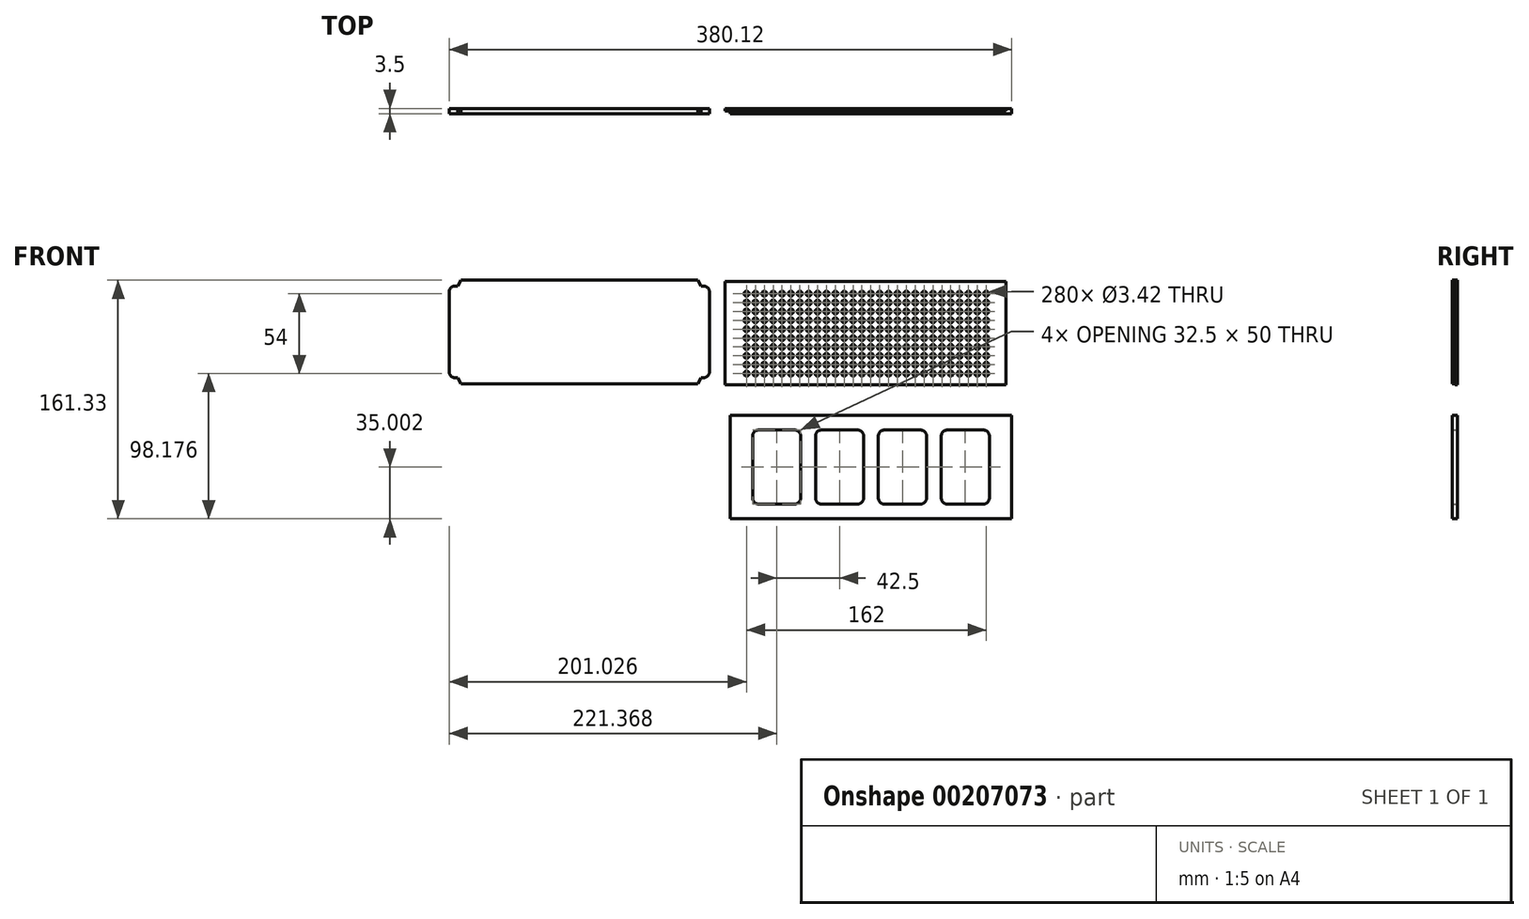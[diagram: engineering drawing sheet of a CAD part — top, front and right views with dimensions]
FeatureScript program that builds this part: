
annotation { "Feature Type Name" : "Feature", "Feature Type Description" : "" }
export const myFeature = defineFeature(function(context is Context, id is Id, definition is map)
    precondition{}
    {
        {
            var Q0;
            Q0=qCreatedBy(makeId("Front.planeOp"),FACE);
            var sketch = newSketch(context, id + "F0", { "sketchPlane" : qUnion([Q0])});
            skLineSegment(sketch, "E0", {"start": v(-6.1, -37) * mm, "end": v(73.9, -37) * mm});
            skLineSegment(sketch, "E1", {"start": v(73.9, -37) * mm, "end": v(76.2, -33) * mm});
            skLineSegment(sketch, "E2", {"start": v(76.2, -33) * mm, "end": v(77.9, -33) * mm});
            skLineSegment(sketch, "E3", {"start": v(77.9, -33) * mm, "end": v(77.9, -33) * mm});
            skLineSegment(sketch, "E4", {"start": v(81.9, -29) * mm, "end": v(81.9, -29) * mm});
            skLineSegment(sketch, "E5", {"start": v(81.9, -29) * mm, "end": v(81.9, 25) * mm});
            skLineSegment(sketch, "E6", {"start": v(77.9, 29) * mm, "end": v(77.9, 29) * mm});
            skLineSegment(sketch, "E7", {"start": v(77.9, 29) * mm, "end": v(76.2, 29) * mm});
            skLineSegment(sketch, "E8", {"start": v(76.2, 29) * mm, "end": v(73.9, 33) * mm});
            skLineSegment(sketch, "E9", {"start": v(73.9, 33) * mm, "end": v(-6.1, 33) * mm});
            skLineSegment(sketch, "E10", {"start": v(-6.1, 33) * mm, "end": v(-6.1, -37) * mm});
            skPoint(sketch, "E11.visualSharp", {"position": v(81.9, -33) * mm});
            skArc(sketch, "E11.filletArc", {"start": v(77.9, -33) * mm, "mid": v(80.72, -31.83) * mm, "end": v(81.9, -29) * mm});
            skArc(sketch, "E12.filletArc", {"start": v(81.9, 25) * mm, "mid": v(80.72, 27.83) * mm, "end": v(77.9, 29) * mm});
            skSolve(sketch);
        }
        {
            var Q0;
            Q0=makeQuery(id+"F0.imprint","IMPRINT",FACE,{"disambiguationData":[TD([[makeQuery(id+"F0.imprint","IMPRINT",EDGE,{"derivedFrom":sQuery(id+"F0.wireOp",EDGE,"E0")}),1.0]])]});
            extrude(context, id + "F1", {"entities" : qUnion([Q0]), "depth" : 3.5 * mm});
        }
        {
            var Q0;
            Q0=makeQuery(id+"F1.opExtrude","SWEPT_BODY",BODY,{"disambiguationData":[OSD([sQuery(id+"F0.wireOp",EDGE,"E0"),sQuery(id+"F0.wireOp",EDGE,"E1"),sQuery(id+"F0.wireOp",EDGE,"E2"),sQuery(id+"F0.wireOp",EDGE,"E5"),sQuery(id+"F0.wireOp",EDGE,"E7"),sQuery(id+"F0.wireOp",EDGE,"E8"),sQuery(id+"F0.wireOp",EDGE,"E9"),sQuery(id+"F0.wireOp",EDGE,"E10"),sQuery(id+"F0.wireOp",EDGE,"E11.filletArc"),sQuery(id+"F0.wireOp",EDGE,"E12.filletArc")])]});
            var Q1;
            Q1=makeQuery(id+"F1.opExtrude","SWEPT_FACE",FACE,{"disambiguationData":[OSD([sQuery(id+"F0.wireOp",EDGE,"E10")])]});
            mirror(context, id + "F2", {"operationType" : NewBodyOperationType.ADD, "entities" : qUnion([Q0]), "mirrorPlane" : qUnion([Q1])});
        }
        {
            var Q0;
            Q0=qCreatedBy(makeId("Front.planeOp"),FACE);
            var sketch = newSketch(context, id + "F3", { "sketchPlane" : qUnion([Q0])});
            skLineSegment(sketch, "E13.bottom", {"start": v(92.39, 32.26) * mm, "end": v(282.39, 32.26) * mm});
            skLineSegment(sketch, "E13.top", {"start": v(92.39, -37.74) * mm, "end": v(282.39, -37.74) * mm});
            skLineSegment(sketch, "E13.left", {"start": v(92.39, 32.26) * mm, "end": v(92.39, -37.74) * mm});
            skLineSegment(sketch, "E13.right", {"start": v(282.39, 32.26) * mm, "end": v(282.39, -37.74) * mm});
            skSolve(sketch);
        }
        {
            var Q0;
            Q0=makeQuery(id+"F3.imprint","IMPRINT",FACE,{"disambiguationData":[TD([[makeQuery(id+"F3.imprint","IMPRINT",EDGE,{"derivedFrom":sQuery(id+"F3.wireOp",EDGE,"E13.bottom")}),-1.0]])]});
            extrude(context, id + "F4", {"entities" : qUnion([Q0]), "depth" : 1.5 * mm});
        }
        {
            var Q0;
            Q0=makeQuery(id+"F4.opExtrude","CAP_FACE",FACE,{"disambiguationData":[OSD([sQuery(id+"F3.wireOp",EDGE,"E13.bottom"),sQuery(id+"F3.wireOp",EDGE,"E13.top"),sQuery(id+"F3.wireOp",EDGE,"E13.left"),sQuery(id+"F3.wireOp",EDGE,"E13.right")])],"isStart":false});
            var sketch = newSketch(context, id + "F5", { "sketchPlane" : qUnion([Q0])});
            skCircle(sketch, "E14", {"center": v(106.92, 23.85) * mm, "radius": 1.7 * mm});
            skCircle(sketch, "E15.0.1.0", {"center": v(106.92, 17.85) * mm, "radius": 1.7 * mm});
            skCircle(sketch, "E15.0.2.0", {"center": v(106.92, 11.85) * mm, "radius": 1.7 * mm});
            skCircle(sketch, "E15.0.3.0", {"center": v(106.92, 5.85) * mm, "radius": 1.7 * mm});
            skCircle(sketch, "E15.0.4.0", {"center": v(106.92, -0.15) * mm, "radius": 1.7 * mm});
            skCircle(sketch, "E15.0.5.0", {"center": v(106.92, -6.15) * mm, "radius": 1.7 * mm});
            skCircle(sketch, "E15.0.6.0", {"center": v(106.92, -12.15) * mm, "radius": 1.7 * mm});
            skCircle(sketch, "E15.0.7.0", {"center": v(106.92, -18.15) * mm, "radius": 1.7 * mm});
            skCircle(sketch, "E15.0.8.0", {"center": v(106.92, -24.15) * mm, "radius": 1.7 * mm});
            skCircle(sketch, "E15.0.9.0", {"center": v(106.92, -30.15) * mm, "radius": 1.7 * mm});
            skCircle(sketch, "E15.1.0.0", {"center": v(112.92, 23.85) * mm, "radius": 1.7 * mm});
            skCircle(sketch, "E15.1.1.0", {"center": v(112.92, 17.85) * mm, "radius": 1.7 * mm});
            skCircle(sketch, "E15.1.2.0", {"center": v(112.92, 11.85) * mm, "radius": 1.7 * mm});
            skCircle(sketch, "E15.1.3.0", {"center": v(112.92, 5.85) * mm, "radius": 1.7 * mm});
            skCircle(sketch, "E15.1.4.0", {"center": v(112.92, -0.15) * mm, "radius": 1.7 * mm});
            skCircle(sketch, "E15.1.5.0", {"center": v(112.92, -6.15) * mm, "radius": 1.7 * mm});
            skCircle(sketch, "E15.1.6.0", {"center": v(112.92, -12.15) * mm, "radius": 1.7 * mm});
            skCircle(sketch, "E15.1.7.0", {"center": v(112.92, -18.15) * mm, "radius": 1.7 * mm});
            skCircle(sketch, "E15.1.8.0", {"center": v(112.92, -24.15) * mm, "radius": 1.7 * mm});
            skCircle(sketch, "E15.1.9.0", {"center": v(112.92, -30.15) * mm, "radius": 1.7 * mm});
            skCircle(sketch, "E15.2.0.0", {"center": v(118.92, 23.85) * mm, "radius": 1.7 * mm});
            skCircle(sketch, "E15.2.1.0", {"center": v(118.92, 17.85) * mm, "radius": 1.7 * mm});
            skCircle(sketch, "E15.2.2.0", {"center": v(118.92, 11.85) * mm, "radius": 1.7 * mm});
            skCircle(sketch, "E15.2.3.0", {"center": v(118.92, 5.85) * mm, "radius": 1.7 * mm});
            skCircle(sketch, "E15.2.4.0", {"center": v(118.92, -0.15) * mm, "radius": 1.7 * mm});
            skCircle(sketch, "E15.2.5.0", {"center": v(118.92, -6.15) * mm, "radius": 1.7 * mm});
            skCircle(sketch, "E15.2.6.0", {"center": v(118.92, -12.15) * mm, "radius": 1.7 * mm});
            skCircle(sketch, "E15.2.7.0", {"center": v(118.92, -18.15) * mm, "radius": 1.7 * mm});
            skCircle(sketch, "E15.2.8.0", {"center": v(118.92, -24.15) * mm, "radius": 1.7 * mm});
            skCircle(sketch, "E15.2.9.0", {"center": v(118.92, -30.15) * mm, "radius": 1.7 * mm});
            skCircle(sketch, "E15.3.0.0", {"center": v(124.92, 23.85) * mm, "radius": 1.7 * mm});
            skCircle(sketch, "E15.3.1.0", {"center": v(124.92, 17.85) * mm, "radius": 1.7 * mm});
            skCircle(sketch, "E15.3.2.0", {"center": v(124.92, 11.85) * mm, "radius": 1.7 * mm});
            skCircle(sketch, "E15.3.3.0", {"center": v(124.92, 5.85) * mm, "radius": 1.7 * mm});
            skCircle(sketch, "E15.3.4.0", {"center": v(124.92, -0.15) * mm, "radius": 1.7 * mm});
            skCircle(sketch, "E15.3.5.0", {"center": v(124.92, -6.15) * mm, "radius": 1.7 * mm});
            skCircle(sketch, "E15.3.6.0", {"center": v(124.92, -12.15) * mm, "radius": 1.7 * mm});
            skCircle(sketch, "E15.3.7.0", {"center": v(124.92, -18.15) * mm, "radius": 1.7 * mm});
            skCircle(sketch, "E15.3.8.0", {"center": v(124.92, -24.15) * mm, "radius": 1.7 * mm});
            skCircle(sketch, "E15.3.9.0", {"center": v(124.92, -30.15) * mm, "radius": 1.7 * mm});
            skCircle(sketch, "E15.4.0.0", {"center": v(130.92, 23.85) * mm, "radius": 1.7 * mm});
            skCircle(sketch, "E15.4.1.0", {"center": v(130.92, 17.85) * mm, "radius": 1.7 * mm});
            skCircle(sketch, "E15.4.2.0", {"center": v(130.92, 11.85) * mm, "radius": 1.7 * mm});
            skCircle(sketch, "E15.4.3.0", {"center": v(130.92, 5.85) * mm, "radius": 1.7 * mm});
            skCircle(sketch, "E15.4.4.0", {"center": v(130.92, -0.15) * mm, "radius": 1.7 * mm});
            skCircle(sketch, "E15.4.5.0", {"center": v(130.92, -6.15) * mm, "radius": 1.7 * mm});
            skCircle(sketch, "E15.4.6.0", {"center": v(130.92, -12.15) * mm, "radius": 1.7 * mm});
            skCircle(sketch, "E15.4.7.0", {"center": v(130.92, -18.15) * mm, "radius": 1.7 * mm});
            skCircle(sketch, "E15.4.8.0", {"center": v(130.92, -24.15) * mm, "radius": 1.7 * mm});
            skCircle(sketch, "E15.4.9.0", {"center": v(130.92, -30.15) * mm, "radius": 1.7 * mm});
            skCircle(sketch, "E15.5.0.0", {"center": v(136.92, 23.85) * mm, "radius": 1.7 * mm});
            skCircle(sketch, "E15.5.1.0", {"center": v(136.92, 17.85) * mm, "radius": 1.7 * mm});
            skCircle(sketch, "E15.5.2.0", {"center": v(136.92, 11.85) * mm, "radius": 1.7 * mm});
            skCircle(sketch, "E15.5.3.0", {"center": v(136.92, 5.85) * mm, "radius": 1.7 * mm});
            skCircle(sketch, "E15.5.4.0", {"center": v(136.92, -0.15) * mm, "radius": 1.7 * mm});
            skCircle(sketch, "E15.5.5.0", {"center": v(136.92, -6.15) * mm, "radius": 1.7 * mm});
            skCircle(sketch, "E15.5.6.0", {"center": v(136.92, -12.15) * mm, "radius": 1.7 * mm});
            skCircle(sketch, "E15.5.7.0", {"center": v(136.92, -18.15) * mm, "radius": 1.7 * mm});
            skCircle(sketch, "E15.5.8.0", {"center": v(136.92, -24.15) * mm, "radius": 1.7 * mm});
            skCircle(sketch, "E15.5.9.0", {"center": v(136.92, -30.15) * mm, "radius": 1.7 * mm});
            skCircle(sketch, "E15.6.0.0", {"center": v(142.92, 23.85) * mm, "radius": 1.7 * mm});
            skCircle(sketch, "E15.6.1.0", {"center": v(142.92, 17.85) * mm, "radius": 1.7 * mm});
            skCircle(sketch, "E15.6.2.0", {"center": v(142.92, 11.85) * mm, "radius": 1.7 * mm});
            skCircle(sketch, "E15.6.3.0", {"center": v(142.92, 5.85) * mm, "radius": 1.7 * mm});
            skCircle(sketch, "E15.6.4.0", {"center": v(142.92, -0.15) * mm, "radius": 1.7 * mm});
            skCircle(sketch, "E15.6.5.0", {"center": v(142.92, -6.15) * mm, "radius": 1.7 * mm});
            skCircle(sketch, "E15.6.6.0", {"center": v(142.92, -12.15) * mm, "radius": 1.7 * mm});
            skCircle(sketch, "E15.6.7.0", {"center": v(142.92, -18.15) * mm, "radius": 1.7 * mm});
            skCircle(sketch, "E15.6.8.0", {"center": v(142.92, -24.15) * mm, "radius": 1.7 * mm});
            skCircle(sketch, "E15.6.9.0", {"center": v(142.92, -30.15) * mm, "radius": 1.7 * mm});
            skCircle(sketch, "E15.7.0.0", {"center": v(148.92, 23.85) * mm, "radius": 1.7 * mm});
            skCircle(sketch, "E15.7.1.0", {"center": v(148.92, 17.85) * mm, "radius": 1.7 * mm});
            skCircle(sketch, "E15.7.2.0", {"center": v(148.92, 11.85) * mm, "radius": 1.7 * mm});
            skCircle(sketch, "E15.7.3.0", {"center": v(148.92, 5.85) * mm, "radius": 1.7 * mm});
            skCircle(sketch, "E15.7.4.0", {"center": v(148.92, -0.15) * mm, "radius": 1.7 * mm});
            skCircle(sketch, "E15.7.5.0", {"center": v(148.92, -6.15) * mm, "radius": 1.7 * mm});
            skCircle(sketch, "E15.7.6.0", {"center": v(148.92, -12.15) * mm, "radius": 1.7 * mm});
            skCircle(sketch, "E15.7.7.0", {"center": v(148.92, -18.15) * mm, "radius": 1.7 * mm});
            skCircle(sketch, "E15.7.8.0", {"center": v(148.92, -24.15) * mm, "radius": 1.7 * mm});
            skCircle(sketch, "E15.7.9.0", {"center": v(148.92, -30.15) * mm, "radius": 1.7 * mm});
            skCircle(sketch, "E15.8.0.0", {"center": v(154.92, 23.85) * mm, "radius": 1.7 * mm});
            skCircle(sketch, "E15.8.1.0", {"center": v(154.92, 17.85) * mm, "radius": 1.7 * mm});
            skCircle(sketch, "E15.8.2.0", {"center": v(154.92, 11.85) * mm, "radius": 1.7 * mm});
            skCircle(sketch, "E15.8.3.0", {"center": v(154.92, 5.85) * mm, "radius": 1.7 * mm});
            skCircle(sketch, "E15.8.4.0", {"center": v(154.92, -0.15) * mm, "radius": 1.7 * mm});
            skCircle(sketch, "E15.8.5.0", {"center": v(154.92, -6.15) * mm, "radius": 1.7 * mm});
            skCircle(sketch, "E15.8.6.0", {"center": v(154.92, -12.15) * mm, "radius": 1.7 * mm});
            skCircle(sketch, "E15.8.7.0", {"center": v(154.92, -18.15) * mm, "radius": 1.7 * mm});
            skCircle(sketch, "E15.8.8.0", {"center": v(154.92, -24.15) * mm, "radius": 1.7 * mm});
            skCircle(sketch, "E15.8.9.0", {"center": v(154.92, -30.15) * mm, "radius": 1.7 * mm});
            skCircle(sketch, "E15.9.0.0", {"center": v(160.92, 23.85) * mm, "radius": 1.7 * mm});
            skCircle(sketch, "E15.9.1.0", {"center": v(160.92, 17.85) * mm, "radius": 1.7 * mm});
            skCircle(sketch, "E15.9.2.0", {"center": v(160.92, 11.85) * mm, "radius": 1.7 * mm});
            skCircle(sketch, "E15.9.3.0", {"center": v(160.92, 5.85) * mm, "radius": 1.7 * mm});
            skCircle(sketch, "E15.9.4.0", {"center": v(160.92, -0.15) * mm, "radius": 1.7 * mm});
            skCircle(sketch, "E15.9.5.0", {"center": v(160.92, -6.15) * mm, "radius": 1.7 * mm});
            skCircle(sketch, "E15.9.6.0", {"center": v(160.92, -12.15) * mm, "radius": 1.7 * mm});
            skCircle(sketch, "E15.9.7.0", {"center": v(160.92, -18.15) * mm, "radius": 1.7 * mm});
            skCircle(sketch, "E15.9.8.0", {"center": v(160.92, -24.15) * mm, "radius": 1.7 * mm});
            skCircle(sketch, "E15.9.9.0", {"center": v(160.92, -30.15) * mm, "radius": 1.7 * mm});
            skCircle(sketch, "E15.10.0.0", {"center": v(166.92, 23.85) * mm, "radius": 1.7 * mm});
            skCircle(sketch, "E15.10.1.0", {"center": v(166.92, 17.85) * mm, "radius": 1.7 * mm});
            skCircle(sketch, "E15.10.2.0", {"center": v(166.92, 11.85) * mm, "radius": 1.7 * mm});
            skCircle(sketch, "E15.10.3.0", {"center": v(166.92, 5.85) * mm, "radius": 1.7 * mm});
            skCircle(sketch, "E15.10.4.0", {"center": v(166.92, -0.15) * mm, "radius": 1.7 * mm});
            skCircle(sketch, "E15.10.5.0", {"center": v(166.92, -6.15) * mm, "radius": 1.7 * mm});
            skCircle(sketch, "E15.10.6.0", {"center": v(166.92, -12.15) * mm, "radius": 1.7 * mm});
            skCircle(sketch, "E15.10.7.0", {"center": v(166.92, -18.15) * mm, "radius": 1.7 * mm});
            skCircle(sketch, "E15.10.8.0", {"center": v(166.92, -24.15) * mm, "radius": 1.7 * mm});
            skCircle(sketch, "E15.10.9.0", {"center": v(166.92, -30.15) * mm, "radius": 1.7 * mm});
            skCircle(sketch, "E15.11.0.0", {"center": v(172.92, 23.85) * mm, "radius": 1.7 * mm});
            skCircle(sketch, "E15.11.1.0", {"center": v(172.92, 17.85) * mm, "radius": 1.7 * mm});
            skCircle(sketch, "E15.11.2.0", {"center": v(172.92, 11.85) * mm, "radius": 1.7 * mm});
            skCircle(sketch, "E15.11.3.0", {"center": v(172.92, 5.85) * mm, "radius": 1.7 * mm});
            skCircle(sketch, "E15.11.4.0", {"center": v(172.92, -0.15) * mm, "radius": 1.7 * mm});
            skCircle(sketch, "E15.11.5.0", {"center": v(172.92, -6.15) * mm, "radius": 1.7 * mm});
            skCircle(sketch, "E15.11.6.0", {"center": v(172.92, -12.15) * mm, "radius": 1.7 * mm});
            skCircle(sketch, "E15.11.7.0", {"center": v(172.92, -18.15) * mm, "radius": 1.7 * mm});
            skCircle(sketch, "E15.11.8.0", {"center": v(172.92, -24.15) * mm, "radius": 1.7 * mm});
            skCircle(sketch, "E15.11.9.0", {"center": v(172.92, -30.15) * mm, "radius": 1.7 * mm});
            skCircle(sketch, "E15.12.0.0", {"center": v(178.92, 23.85) * mm, "radius": 1.7 * mm});
            skCircle(sketch, "E15.12.1.0", {"center": v(178.92, 17.85) * mm, "radius": 1.7 * mm});
            skCircle(sketch, "E15.12.2.0", {"center": v(178.92, 11.85) * mm, "radius": 1.7 * mm});
            skCircle(sketch, "E15.12.3.0", {"center": v(178.92, 5.85) * mm, "radius": 1.7 * mm});
            skCircle(sketch, "E15.12.4.0", {"center": v(178.92, -0.15) * mm, "radius": 1.7 * mm});
            skCircle(sketch, "E15.12.5.0", {"center": v(178.92, -6.15) * mm, "radius": 1.7 * mm});
            skCircle(sketch, "E15.12.6.0", {"center": v(178.92, -12.15) * mm, "radius": 1.7 * mm});
            skCircle(sketch, "E15.12.7.0", {"center": v(178.92, -18.15) * mm, "radius": 1.7 * mm});
            skCircle(sketch, "E15.12.8.0", {"center": v(178.92, -24.15) * mm, "radius": 1.7 * mm});
            skCircle(sketch, "E15.12.9.0", {"center": v(178.92, -30.15) * mm, "radius": 1.7 * mm});
            skCircle(sketch, "E15.13.0.0", {"center": v(184.92, 23.85) * mm, "radius": 1.7 * mm});
            skCircle(sketch, "E15.13.1.0", {"center": v(184.92, 17.85) * mm, "radius": 1.7 * mm});
            skCircle(sketch, "E15.13.2.0", {"center": v(184.92, 11.85) * mm, "radius": 1.7 * mm});
            skCircle(sketch, "E15.13.3.0", {"center": v(184.92, 5.85) * mm, "radius": 1.7 * mm});
            skCircle(sketch, "E15.13.4.0", {"center": v(184.92, -0.15) * mm, "radius": 1.7 * mm});
            skCircle(sketch, "E15.13.5.0", {"center": v(184.92, -6.15) * mm, "radius": 1.7 * mm});
            skCircle(sketch, "E15.13.6.0", {"center": v(184.92, -12.15) * mm, "radius": 1.7 * mm});
            skCircle(sketch, "E15.13.7.0", {"center": v(184.92, -18.15) * mm, "radius": 1.7 * mm});
            skCircle(sketch, "E15.13.8.0", {"center": v(184.92, -24.15) * mm, "radius": 1.7 * mm});
            skCircle(sketch, "E15.13.9.0", {"center": v(184.92, -30.15) * mm, "radius": 1.7 * mm});
            skCircle(sketch, "E15.14.0.0", {"center": v(190.92, 23.85) * mm, "radius": 1.7 * mm});
            skCircle(sketch, "E15.14.1.0", {"center": v(190.92, 17.85) * mm, "radius": 1.7 * mm});
            skCircle(sketch, "E15.14.2.0", {"center": v(190.92, 11.85) * mm, "radius": 1.7 * mm});
            skCircle(sketch, "E15.14.3.0", {"center": v(190.92, 5.85) * mm, "radius": 1.7 * mm});
            skCircle(sketch, "E15.14.4.0", {"center": v(190.92, -0.15) * mm, "radius": 1.7 * mm});
            skCircle(sketch, "E15.14.5.0", {"center": v(190.92, -6.15) * mm, "radius": 1.7 * mm});
            skCircle(sketch, "E15.14.6.0", {"center": v(190.92, -12.15) * mm, "radius": 1.7 * mm});
            skCircle(sketch, "E15.14.7.0", {"center": v(190.92, -18.15) * mm, "radius": 1.7 * mm});
            skCircle(sketch, "E15.14.8.0", {"center": v(190.92, -24.15) * mm, "radius": 1.7 * mm});
            skCircle(sketch, "E15.14.9.0", {"center": v(190.92, -30.15) * mm, "radius": 1.7 * mm});
            skCircle(sketch, "E15.15.0.0", {"center": v(196.92, 23.85) * mm, "radius": 1.7 * mm});
            skCircle(sketch, "E15.15.1.0", {"center": v(196.92, 17.85) * mm, "radius": 1.7 * mm});
            skCircle(sketch, "E15.15.2.0", {"center": v(196.92, 11.85) * mm, "radius": 1.7 * mm});
            skCircle(sketch, "E15.15.3.0", {"center": v(196.92, 5.85) * mm, "radius": 1.7 * mm});
            skCircle(sketch, "E15.15.4.0", {"center": v(196.92, -0.15) * mm, "radius": 1.7 * mm});
            skCircle(sketch, "E15.15.5.0", {"center": v(196.92, -6.15) * mm, "radius": 1.7 * mm});
            skCircle(sketch, "E15.15.6.0", {"center": v(196.92, -12.15) * mm, "radius": 1.7 * mm});
            skCircle(sketch, "E15.15.7.0", {"center": v(196.92, -18.15) * mm, "radius": 1.7 * mm});
            skCircle(sketch, "E15.15.8.0", {"center": v(196.92, -24.15) * mm, "radius": 1.7 * mm});
            skCircle(sketch, "E15.15.9.0", {"center": v(196.92, -30.15) * mm, "radius": 1.7 * mm});
            skCircle(sketch, "E15.16.0.0", {"center": v(202.92, 23.85) * mm, "radius": 1.7 * mm});
            skCircle(sketch, "E15.16.1.0", {"center": v(202.92, 17.85) * mm, "radius": 1.7 * mm});
            skCircle(sketch, "E15.16.2.0", {"center": v(202.92, 11.85) * mm, "radius": 1.7 * mm});
            skCircle(sketch, "E15.16.3.0", {"center": v(202.92, 5.85) * mm, "radius": 1.7 * mm});
            skCircle(sketch, "E15.16.4.0", {"center": v(202.92, -0.15) * mm, "radius": 1.7 * mm});
            skCircle(sketch, "E15.16.5.0", {"center": v(202.92, -6.15) * mm, "radius": 1.7 * mm});
            skCircle(sketch, "E15.16.6.0", {"center": v(202.92, -12.15) * mm, "radius": 1.7 * mm});
            skCircle(sketch, "E15.16.7.0", {"center": v(202.92, -18.15) * mm, "radius": 1.7 * mm});
            skCircle(sketch, "E15.16.8.0", {"center": v(202.92, -24.15) * mm, "radius": 1.7 * mm});
            skCircle(sketch, "E15.16.9.0", {"center": v(202.92, -30.15) * mm, "radius": 1.7 * mm});
            skCircle(sketch, "E15.17.0.0", {"center": v(208.92, 23.85) * mm, "radius": 1.7 * mm});
            skCircle(sketch, "E15.17.1.0", {"center": v(208.92, 17.85) * mm, "radius": 1.7 * mm});
            skCircle(sketch, "E15.17.2.0", {"center": v(208.92, 11.85) * mm, "radius": 1.7 * mm});
            skCircle(sketch, "E15.17.3.0", {"center": v(208.92, 5.85) * mm, "radius": 1.7 * mm});
            skCircle(sketch, "E15.17.4.0", {"center": v(208.92, -0.15) * mm, "radius": 1.7 * mm});
            skCircle(sketch, "E15.17.5.0", {"center": v(208.92, -6.15) * mm, "radius": 1.7 * mm});
            skCircle(sketch, "E15.17.6.0", {"center": v(208.92, -12.15) * mm, "radius": 1.7 * mm});
            skCircle(sketch, "E15.17.7.0", {"center": v(208.92, -18.15) * mm, "radius": 1.7 * mm});
            skCircle(sketch, "E15.17.8.0", {"center": v(208.92, -24.15) * mm, "radius": 1.7 * mm});
            skCircle(sketch, "E15.17.9.0", {"center": v(208.92, -30.15) * mm, "radius": 1.7 * mm});
            skCircle(sketch, "E15.18.0.0", {"center": v(214.92, 23.85) * mm, "radius": 1.7 * mm});
            skCircle(sketch, "E15.18.1.0", {"center": v(214.92, 17.85) * mm, "radius": 1.7 * mm});
            skCircle(sketch, "E15.18.2.0", {"center": v(214.92, 11.85) * mm, "radius": 1.7 * mm});
            skCircle(sketch, "E15.18.3.0", {"center": v(214.92, 5.85) * mm, "radius": 1.7 * mm});
            skCircle(sketch, "E15.18.4.0", {"center": v(214.92, -0.15) * mm, "radius": 1.7 * mm});
            skCircle(sketch, "E15.18.5.0", {"center": v(214.92, -6.15) * mm, "radius": 1.7 * mm});
            skCircle(sketch, "E15.18.6.0", {"center": v(214.92, -12.15) * mm, "radius": 1.7 * mm});
            skCircle(sketch, "E15.18.7.0", {"center": v(214.92, -18.15) * mm, "radius": 1.7 * mm});
            skCircle(sketch, "E15.18.8.0", {"center": v(214.92, -24.15) * mm, "radius": 1.7 * mm});
            skCircle(sketch, "E15.18.9.0", {"center": v(214.92, -30.15) * mm, "radius": 1.7 * mm});
            skCircle(sketch, "E15.19.0.0", {"center": v(220.92, 23.85) * mm, "radius": 1.7 * mm});
            skCircle(sketch, "E15.19.1.0", {"center": v(220.92, 17.85) * mm, "radius": 1.7 * mm});
            skCircle(sketch, "E15.19.2.0", {"center": v(220.92, 11.85) * mm, "radius": 1.7 * mm});
            skCircle(sketch, "E15.19.3.0", {"center": v(220.92, 5.85) * mm, "radius": 1.7 * mm});
            skCircle(sketch, "E15.19.4.0", {"center": v(220.92, -0.15) * mm, "radius": 1.7 * mm});
            skCircle(sketch, "E15.19.5.0", {"center": v(220.92, -6.15) * mm, "radius": 1.7 * mm});
            skCircle(sketch, "E15.19.6.0", {"center": v(220.92, -12.15) * mm, "radius": 1.7 * mm});
            skCircle(sketch, "E15.19.7.0", {"center": v(220.92, -18.15) * mm, "radius": 1.7 * mm});
            skCircle(sketch, "E15.19.8.0", {"center": v(220.92, -24.15) * mm, "radius": 1.7 * mm});
            skCircle(sketch, "E15.19.9.0", {"center": v(220.92, -30.15) * mm, "radius": 1.7 * mm});
            skCircle(sketch, "E15.20.0.0", {"center": v(226.92, 23.85) * mm, "radius": 1.7 * mm});
            skCircle(sketch, "E15.20.1.0", {"center": v(226.92, 17.85) * mm, "radius": 1.7 * mm});
            skCircle(sketch, "E15.20.2.0", {"center": v(226.92, 11.85) * mm, "radius": 1.7 * mm});
            skCircle(sketch, "E15.20.3.0", {"center": v(226.92, 5.85) * mm, "radius": 1.7 * mm});
            skCircle(sketch, "E15.20.4.0", {"center": v(226.92, -0.15) * mm, "radius": 1.7 * mm});
            skCircle(sketch, "E15.20.5.0", {"center": v(226.92, -6.15) * mm, "radius": 1.7 * mm});
            skCircle(sketch, "E15.20.6.0", {"center": v(226.92, -12.15) * mm, "radius": 1.7 * mm});
            skCircle(sketch, "E15.20.7.0", {"center": v(226.92, -18.15) * mm, "radius": 1.7 * mm});
            skCircle(sketch, "E15.20.8.0", {"center": v(226.92, -24.15) * mm, "radius": 1.7 * mm});
            skCircle(sketch, "E15.20.9.0", {"center": v(226.92, -30.15) * mm, "radius": 1.7 * mm});
            skCircle(sketch, "E15.21.0.0", {"center": v(232.92, 23.85) * mm, "radius": 1.7 * mm});
            skCircle(sketch, "E15.21.1.0", {"center": v(232.92, 17.85) * mm, "radius": 1.7 * mm});
            skCircle(sketch, "E15.21.2.0", {"center": v(232.92, 11.85) * mm, "radius": 1.7 * mm});
            skCircle(sketch, "E15.21.3.0", {"center": v(232.92, 5.85) * mm, "radius": 1.7 * mm});
            skCircle(sketch, "E15.21.4.0", {"center": v(232.92, -0.15) * mm, "radius": 1.7 * mm});
            skCircle(sketch, "E15.21.5.0", {"center": v(232.92, -6.15) * mm, "radius": 1.7 * mm});
            skCircle(sketch, "E15.21.6.0", {"center": v(232.92, -12.15) * mm, "radius": 1.7 * mm});
            skCircle(sketch, "E15.21.7.0", {"center": v(232.92, -18.15) * mm, "radius": 1.7 * mm});
            skCircle(sketch, "E15.21.8.0", {"center": v(232.92, -24.15) * mm, "radius": 1.7 * mm});
            skCircle(sketch, "E15.21.9.0", {"center": v(232.92, -30.15) * mm, "radius": 1.7 * mm});
            skCircle(sketch, "E15.22.0.0", {"center": v(238.92, 23.85) * mm, "radius": 1.7 * mm});
            skCircle(sketch, "E15.22.1.0", {"center": v(238.92, 17.85) * mm, "radius": 1.7 * mm});
            skCircle(sketch, "E15.22.2.0", {"center": v(238.92, 11.85) * mm, "radius": 1.7 * mm});
            skCircle(sketch, "E15.22.3.0", {"center": v(238.92, 5.85) * mm, "radius": 1.7 * mm});
            skCircle(sketch, "E15.22.4.0", {"center": v(238.92, -0.15) * mm, "radius": 1.7 * mm});
            skCircle(sketch, "E15.22.5.0", {"center": v(238.92, -6.15) * mm, "radius": 1.7 * mm});
            skCircle(sketch, "E15.22.6.0", {"center": v(238.92, -12.15) * mm, "radius": 1.7 * mm});
            skCircle(sketch, "E15.22.7.0", {"center": v(238.92, -18.15) * mm, "radius": 1.7 * mm});
            skCircle(sketch, "E15.22.8.0", {"center": v(238.92, -24.15) * mm, "radius": 1.7 * mm});
            skCircle(sketch, "E15.22.9.0", {"center": v(238.92, -30.15) * mm, "radius": 1.7 * mm});
            skCircle(sketch, "E15.23.0.0", {"center": v(244.92, 23.85) * mm, "radius": 1.7 * mm});
            skCircle(sketch, "E15.23.1.0", {"center": v(244.92, 17.85) * mm, "radius": 1.7 * mm});
            skCircle(sketch, "E15.23.2.0", {"center": v(244.92, 11.85) * mm, "radius": 1.7 * mm});
            skCircle(sketch, "E15.23.3.0", {"center": v(244.92, 5.85) * mm, "radius": 1.7 * mm});
            skCircle(sketch, "E15.23.4.0", {"center": v(244.92, -0.15) * mm, "radius": 1.7 * mm});
            skCircle(sketch, "E15.23.5.0", {"center": v(244.92, -6.15) * mm, "radius": 1.7 * mm});
            skCircle(sketch, "E15.23.6.0", {"center": v(244.92, -12.15) * mm, "radius": 1.7 * mm});
            skCircle(sketch, "E15.23.7.0", {"center": v(244.92, -18.15) * mm, "radius": 1.7 * mm});
            skCircle(sketch, "E15.23.8.0", {"center": v(244.92, -24.15) * mm, "radius": 1.7 * mm});
            skCircle(sketch, "E15.23.9.0", {"center": v(244.92, -30.15) * mm, "radius": 1.7 * mm});
            skCircle(sketch, "E15.24.0.0", {"center": v(250.92, 23.85) * mm, "radius": 1.7 * mm});
            skCircle(sketch, "E15.24.1.0", {"center": v(250.92, 17.85) * mm, "radius": 1.7 * mm});
            skCircle(sketch, "E15.24.2.0", {"center": v(250.92, 11.85) * mm, "radius": 1.7 * mm});
            skCircle(sketch, "E15.24.3.0", {"center": v(250.92, 5.85) * mm, "radius": 1.7 * mm});
            skCircle(sketch, "E15.24.4.0", {"center": v(250.92, -0.15) * mm, "radius": 1.7 * mm});
            skCircle(sketch, "E15.24.5.0", {"center": v(250.92, -6.15) * mm, "radius": 1.7 * mm});
            skCircle(sketch, "E15.24.6.0", {"center": v(250.92, -12.15) * mm, "radius": 1.7 * mm});
            skCircle(sketch, "E15.24.7.0", {"center": v(250.92, -18.15) * mm, "radius": 1.7 * mm});
            skCircle(sketch, "E15.24.8.0", {"center": v(250.92, -24.15) * mm, "radius": 1.7 * mm});
            skCircle(sketch, "E15.24.9.0", {"center": v(250.92, -30.15) * mm, "radius": 1.7 * mm});
            skCircle(sketch, "E15.25.0.0", {"center": v(256.92, 23.85) * mm, "radius": 1.7 * mm});
            skCircle(sketch, "E15.25.1.0", {"center": v(256.92, 17.85) * mm, "radius": 1.7 * mm});
            skCircle(sketch, "E15.25.2.0", {"center": v(256.92, 11.85) * mm, "radius": 1.7 * mm});
            skCircle(sketch, "E15.25.3.0", {"center": v(256.92, 5.85) * mm, "radius": 1.7 * mm});
            skCircle(sketch, "E15.25.4.0", {"center": v(256.92, -0.15) * mm, "radius": 1.7 * mm});
            skCircle(sketch, "E15.25.5.0", {"center": v(256.92, -6.15) * mm, "radius": 1.7 * mm});
            skCircle(sketch, "E15.25.6.0", {"center": v(256.92, -12.15) * mm, "radius": 1.7 * mm});
            skCircle(sketch, "E15.25.7.0", {"center": v(256.92, -18.15) * mm, "radius": 1.7 * mm});
            skCircle(sketch, "E15.25.8.0", {"center": v(256.92, -24.15) * mm, "radius": 1.7 * mm});
            skCircle(sketch, "E15.25.9.0", {"center": v(256.92, -30.15) * mm, "radius": 1.7 * mm});
            skCircle(sketch, "E15.26.0.0", {"center": v(262.92, 23.85) * mm, "radius": 1.7 * mm});
            skCircle(sketch, "E15.26.1.0", {"center": v(262.92, 17.85) * mm, "radius": 1.7 * mm});
            skCircle(sketch, "E15.26.2.0", {"center": v(262.92, 11.85) * mm, "radius": 1.7 * mm});
            skCircle(sketch, "E15.26.3.0", {"center": v(262.92, 5.85) * mm, "radius": 1.7 * mm});
            skCircle(sketch, "E15.26.4.0", {"center": v(262.92, -0.15) * mm, "radius": 1.7 * mm});
            skCircle(sketch, "E15.26.5.0", {"center": v(262.92, -6.15) * mm, "radius": 1.7 * mm});
            skCircle(sketch, "E15.26.6.0", {"center": v(262.92, -12.15) * mm, "radius": 1.7 * mm});
            skCircle(sketch, "E15.26.7.0", {"center": v(262.92, -18.15) * mm, "radius": 1.7 * mm});
            skCircle(sketch, "E15.26.8.0", {"center": v(262.92, -24.15) * mm, "radius": 1.7 * mm});
            skCircle(sketch, "E15.26.9.0", {"center": v(262.92, -30.15) * mm, "radius": 1.7 * mm});
            skCircle(sketch, "E15.27.0.0", {"center": v(268.92, 23.85) * mm, "radius": 1.7 * mm});
            skCircle(sketch, "E15.27.1.0", {"center": v(268.92, 17.85) * mm, "radius": 1.7 * mm});
            skCircle(sketch, "E15.27.2.0", {"center": v(268.92, 11.85) * mm, "radius": 1.7 * mm});
            skCircle(sketch, "E15.27.3.0", {"center": v(268.92, 5.85) * mm, "radius": 1.7 * mm});
            skCircle(sketch, "E15.27.4.0", {"center": v(268.92, -0.15) * mm, "radius": 1.7 * mm});
            skCircle(sketch, "E15.27.5.0", {"center": v(268.92, -6.15) * mm, "radius": 1.7 * mm});
            skCircle(sketch, "E15.27.6.0", {"center": v(268.92, -12.15) * mm, "radius": 1.7 * mm});
            skCircle(sketch, "E15.27.7.0", {"center": v(268.92, -18.15) * mm, "radius": 1.7 * mm});
            skCircle(sketch, "E15.27.8.0", {"center": v(268.92, -24.15) * mm, "radius": 1.7 * mm});
            skCircle(sketch, "E15.27.9.0", {"center": v(268.92, -30.15) * mm, "radius": 1.7 * mm});
            skLineSegment(sketch, "E15.direction1", {"start": v(106.92, 23.85) * mm, "end": v(112.92, 23.85) * mm, "construction": true});
            skLineSegment(sketch, "E15.direction2", {"start": v(106.92, 23.85) * mm, "end": v(106.92, 17.85) * mm, "construction": true});
            skSolve(sketch);
        }
        {
            var Q0;
            Q0 = qSketchRegion(id + "F5", true);
            extrude(context, id + "F6", {"entities" : qUnion([Q0]), "operationType" : NewBodyOperationType.REMOVE, "oppositeDirection" : true, "depth" : 25 * mm});
        }
        {
            var Q0;
            Q0=qCreatedBy(makeId("Front.planeOp"),FACE);
            var sketch = newSketch(context, id + "F7", { "sketchPlane" : qUnion([Q0])});
            skLineSegment(sketch, "E16.bottom", {"start": v(96, -58.33) * mm, "end": v(286, -58.33) * mm});
            skLineSegment(sketch, "E16.top", {"start": v(96, -128.33) * mm, "end": v(286, -128.33) * mm});
            skLineSegment(sketch, "E16.left", {"start": v(96, -58.33) * mm, "end": v(96, -128.33) * mm});
            skLineSegment(sketch, "E16.right", {"start": v(286, -58.33) * mm, "end": v(286, -128.33) * mm});
            skLineSegment(sketch, "E17", {"start": v(96, -118.33) * mm, "end": v(111, -118.33) * mm, "construction": true});
            skLineSegment(sketch, "E18.bottom", {"start": v(115, -118.33) * mm, "end": v(139.5, -118.33) * mm});
            skLineSegment(sketch, "E18.top", {"start": v(115, -68.33) * mm, "end": v(139.5, -68.33) * mm});
            skLineSegment(sketch, "E18.left", {"start": v(111, -114.33) * mm, "end": v(111, -72.33) * mm});
            skLineSegment(sketch, "E18.right", {"start": v(143.5, -114.33) * mm, "end": v(143.5, -72.33) * mm});
            skPoint(sketch, "E19.visualSharp", {"position": v(111, -118.33) * mm});
            skArc(sketch, "E19.filletArc", {"start": v(111, -114.33) * mm, "mid": v(112.18, -117.16) * mm, "end": v(115, -118.33) * mm});
            skPoint(sketch, "E20.visualSharp", {"position": v(111, -68.33) * mm});
            skArc(sketch, "E20.filletArc", {"start": v(115, -68.33) * mm, "mid": v(112.18, -69.5) * mm, "end": v(111, -72.33) * mm});
            skPoint(sketch, "E21.visualSharp", {"position": v(143.5, -68.33) * mm});
            skArc(sketch, "E21.filletArc", {"start": v(143.5, -72.33) * mm, "mid": v(142.34, -69.5) * mm, "end": v(139.5, -68.33) * mm});
            skPoint(sketch, "E22.visualSharp", {"position": v(143.5, -118.33) * mm});
            skArc(sketch, "E22.filletArc", {"start": v(139.5, -118.33) * mm, "mid": v(142.34, -117.16) * mm, "end": v(143.5, -114.33) * mm});
            skLineSegment(sketch, "E23.1.0.0", {"start": v(153.5, -114.33) * mm, "end": v(153.5, -72.33) * mm});
            skLineSegment(sketch, "E23.1.0.1", {"start": v(186, -114.33) * mm, "end": v(186, -72.33) * mm});
            skPoint(sketch, "E23.1.0.2", {"position": v(186, -68.33) * mm});
            skLineSegment(sketch, "E23.1.0.3", {"start": v(157.5, -68.33) * mm, "end": v(182, -68.33) * mm});
            skPoint(sketch, "E23.1.0.4", {"position": v(153.5, -68.33) * mm});
            skArc(sketch, "E23.1.0.5", {"start": v(157.5, -68.33) * mm, "mid": v(154.68, -69.5) * mm, "end": v(153.5, -72.33) * mm});
            skArc(sketch, "E23.1.0.6", {"start": v(186, -72.33) * mm, "mid": v(184.84, -69.5) * mm, "end": v(182, -68.33) * mm});
            skLineSegment(sketch, "E23.1.0.7", {"start": v(157.5, -118.33) * mm, "end": v(182, -118.33) * mm});
            skArc(sketch, "E23.1.0.8", {"start": v(153.5, -114.33) * mm, "mid": v(154.68, -117.16) * mm, "end": v(157.5, -118.33) * mm});
            skArc(sketch, "E23.1.0.9", {"start": v(182, -118.33) * mm, "mid": v(184.84, -117.16) * mm, "end": v(186, -114.33) * mm});
            skLineSegment(sketch, "E23.2.0.0", {"start": v(196, -114.33) * mm, "end": v(196, -72.33) * mm});
            skLineSegment(sketch, "E23.2.0.1", {"start": v(228.5, -114.33) * mm, "end": v(228.5, -72.33) * mm});
            skPoint(sketch, "E23.2.0.2", {"position": v(228.5, -68.33) * mm});
            skLineSegment(sketch, "E23.2.0.3", {"start": v(200, -68.33) * mm, "end": v(224.5, -68.33) * mm});
            skPoint(sketch, "E23.2.0.4", {"position": v(196, -68.33) * mm});
            skArc(sketch, "E23.2.0.5", {"start": v(200, -68.33) * mm, "mid": v(197.18, -69.5) * mm, "end": v(196, -72.33) * mm});
            skArc(sketch, "E23.2.0.6", {"start": v(228.5, -72.33) * mm, "mid": v(227.34, -69.5) * mm, "end": v(224.5, -68.33) * mm});
            skLineSegment(sketch, "E23.2.0.7", {"start": v(200, -118.33) * mm, "end": v(224.5, -118.33) * mm});
            skArc(sketch, "E23.2.0.8", {"start": v(196, -114.33) * mm, "mid": v(197.18, -117.16) * mm, "end": v(200, -118.33) * mm});
            skArc(sketch, "E23.2.0.9", {"start": v(224.5, -118.33) * mm, "mid": v(227.34, -117.16) * mm, "end": v(228.5, -114.33) * mm});
            skLineSegment(sketch, "E23.3.0.0", {"start": v(238.5, -114.33) * mm, "end": v(238.5, -72.33) * mm});
            skLineSegment(sketch, "E23.3.0.1", {"start": v(271, -114.33) * mm, "end": v(271, -72.33) * mm});
            skPoint(sketch, "E23.3.0.2", {"position": v(271, -68.33) * mm});
            skLineSegment(sketch, "E23.3.0.3", {"start": v(242.5, -68.33) * mm, "end": v(267, -68.33) * mm});
            skPoint(sketch, "E23.3.0.4", {"position": v(238.5, -68.33) * mm});
            skArc(sketch, "E23.3.0.5", {"start": v(242.5, -68.33) * mm, "mid": v(239.68, -69.5) * mm, "end": v(238.5, -72.33) * mm});
            skArc(sketch, "E23.3.0.6", {"start": v(271, -72.33) * mm, "mid": v(269.84, -69.5) * mm, "end": v(267, -68.33) * mm});
            skLineSegment(sketch, "E23.3.0.7", {"start": v(242.5, -118.33) * mm, "end": v(267, -118.33) * mm});
            skArc(sketch, "E23.3.0.8", {"start": v(238.5, -114.33) * mm, "mid": v(239.68, -117.16) * mm, "end": v(242.5, -118.33) * mm});
            skArc(sketch, "E23.3.0.9", {"start": v(267, -118.33) * mm, "mid": v(269.84, -117.16) * mm, "end": v(271, -114.33) * mm});
            skLineSegment(sketch, "E23.direction1", {"start": v(111, -114.33) * mm, "end": v(153.5, -114.33) * mm, "construction": true});
            skSolve(sketch);
        }
        {
            var Q0;
            Q0=makeQuery(id+"F7.imprint","IMPRINT",FACE,{"disambiguationData":[TD([[makeQuery(id+"F7.imprint","IMPRINT",EDGE,{"derivedFrom":sQuery(id+"F7.wireOp",EDGE,"E16.bottom")}),-1.0]])]});
            extrude(context, id + "F8", {"entities" : qUnion([Q0]), "depth" : 3.5 * mm});
        }
    });
